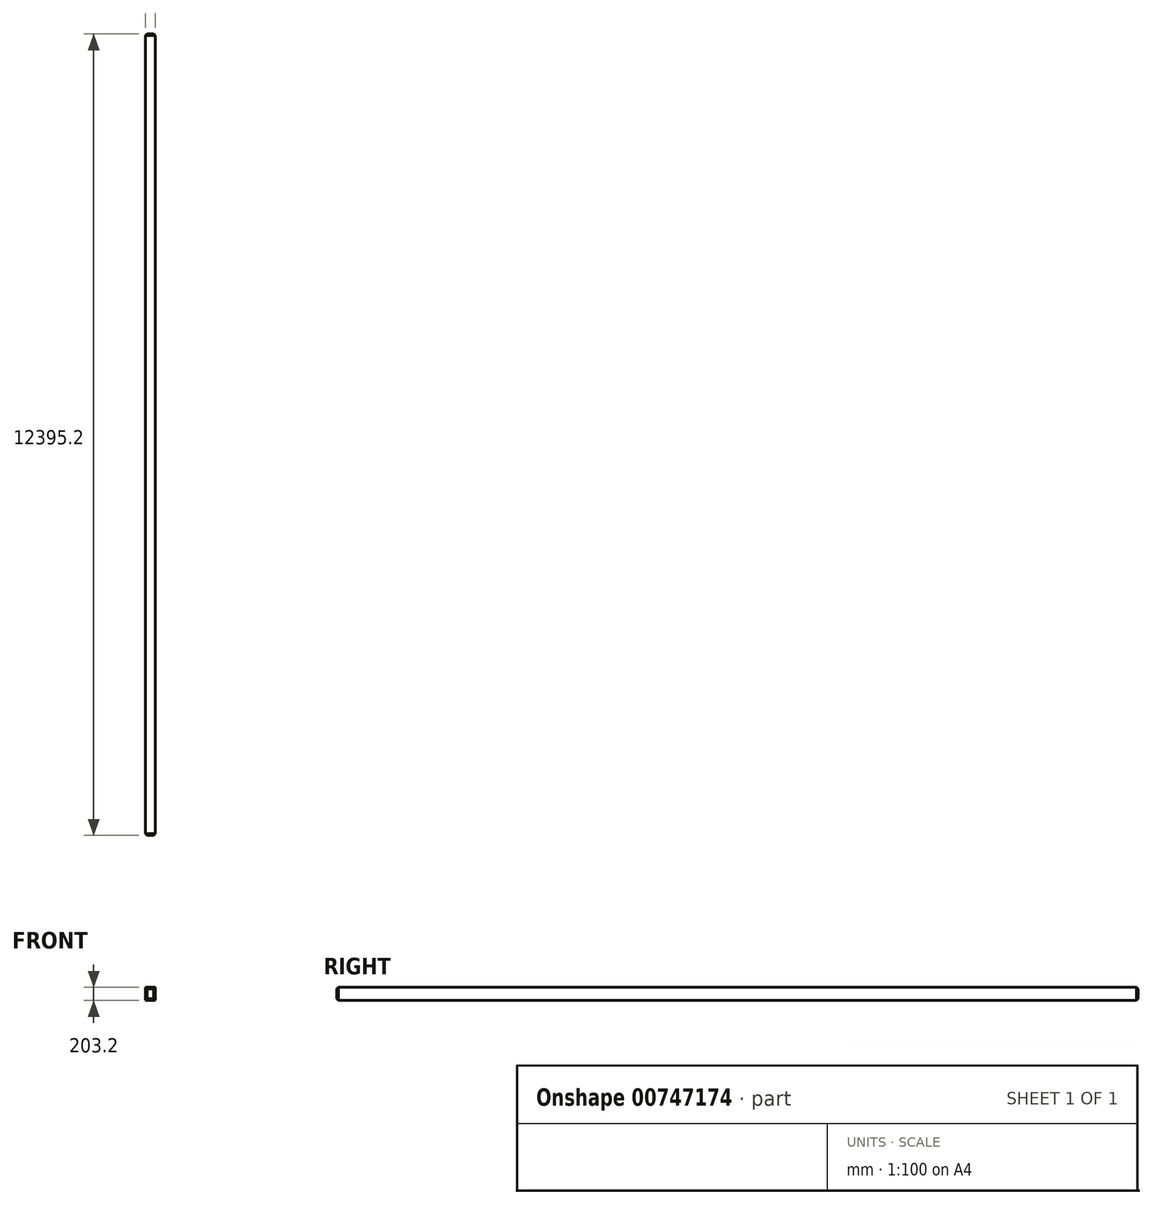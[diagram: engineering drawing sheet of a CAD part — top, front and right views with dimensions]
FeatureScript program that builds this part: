
annotation { "Feature Type Name" : "Feature", "Feature Type Description" : "" }
export const myFeature = defineFeature(function(context is Context, id is Id, definition is map)
    precondition{}
    {
        {
            var Q0;
            Q0=qCreatedBy(makeId("Front.planeOp"),FACE);
            var sketch = newSketch(context, id + "F0", { "sketchPlane" : qUnion([Q0])});
            skLineSegment(sketch, "E0.bottom", {"start": v(-299.1, 0) * mm, "end": v(-146.7, 0) * mm});
            skLineSegment(sketch, "E0.top", {"start": v(-299.1, -203.2) * mm, "end": v(-146.7, -203.2) * mm});
            skLineSegment(sketch, "E0.left", {"start": v(-299.1, 0) * mm, "end": v(-299.1, -203.2) * mm});
            skLineSegment(sketch, "E0.right", {"start": v(-146.7, 0) * mm, "end": v(-146.7, -203.2) * mm});
            skSolve(sketch);
        }
        {
            var Q0;
            Q0 = qSketchRegion(id + "F0", true);
            extrude(context, id + "F1", {"entities" : qUnion([Q0]), "depth" : 12395.2 * mm, "offsetDistance" : 25.4 * mm});
        }
        {
            var Q0;
            Q0=makeQuery(id+"F1.opExtrude","CAP_EDGE",EDGE,{"disambiguationData":[OSD([sQuery(id+"F0.wireOp",EDGE,"E0.right")])],"isStart":false});
            var Q1;
            Q1=makeQuery(id+"F1.opExtrude","CAP_EDGE",EDGE,{"disambiguationData":[OSD([sQuery(id+"F0.wireOp",EDGE,"E0.bottom")])],"isStart":false});
            var Q2;
            Q2=makeQuery(id+"F1.opExtrude","CAP_EDGE",EDGE,{"disambiguationData":[OSD([sQuery(id+"F0.wireOp",EDGE,"E0.left")])],"isStart":false});
            var Q3;
            Q3=makeQuery(id+"F1.opExtrude","CAP_EDGE",EDGE,{"disambiguationData":[OSD([sQuery(id+"F0.wireOp",EDGE,"E0.top")])],"isStart":false});
            chamfer(context, id + "F2", {"entities" : qUnion([Q0, Q1, Q2, Q3]), "width" : 25.4 * mm, "tangentPropagation" : true});
        }
        {
            var Q0;
            Q0=makeQuery(id+"F1.opExtrude","CAP_EDGE",EDGE,{"disambiguationData":[OSD([sQuery(id+"F0.wireOp",EDGE,"E0.bottom")])],"isStart":true});
            var Q1;
            Q1=makeQuery(id+"F1.opExtrude","CAP_EDGE",EDGE,{"disambiguationData":[OSD([sQuery(id+"F0.wireOp",EDGE,"E0.right")])],"isStart":true});
            var Q2;
            Q2=makeQuery(id+"F1.opExtrude","CAP_EDGE",EDGE,{"disambiguationData":[OSD([sQuery(id+"F0.wireOp",EDGE,"E0.top")])],"isStart":true});
            var Q3;
            Q3=makeQuery(id+"F1.opExtrude","CAP_EDGE",EDGE,{"disambiguationData":[OSD([sQuery(id+"F0.wireOp",EDGE,"E0.left")])],"isStart":true});
            chamfer(context, id + "F3", {"entities" : qUnion([Q0, Q1, Q2, Q3]), "width" : 25.4 * mm, "tangentPropagation" : true});
        }
    });
